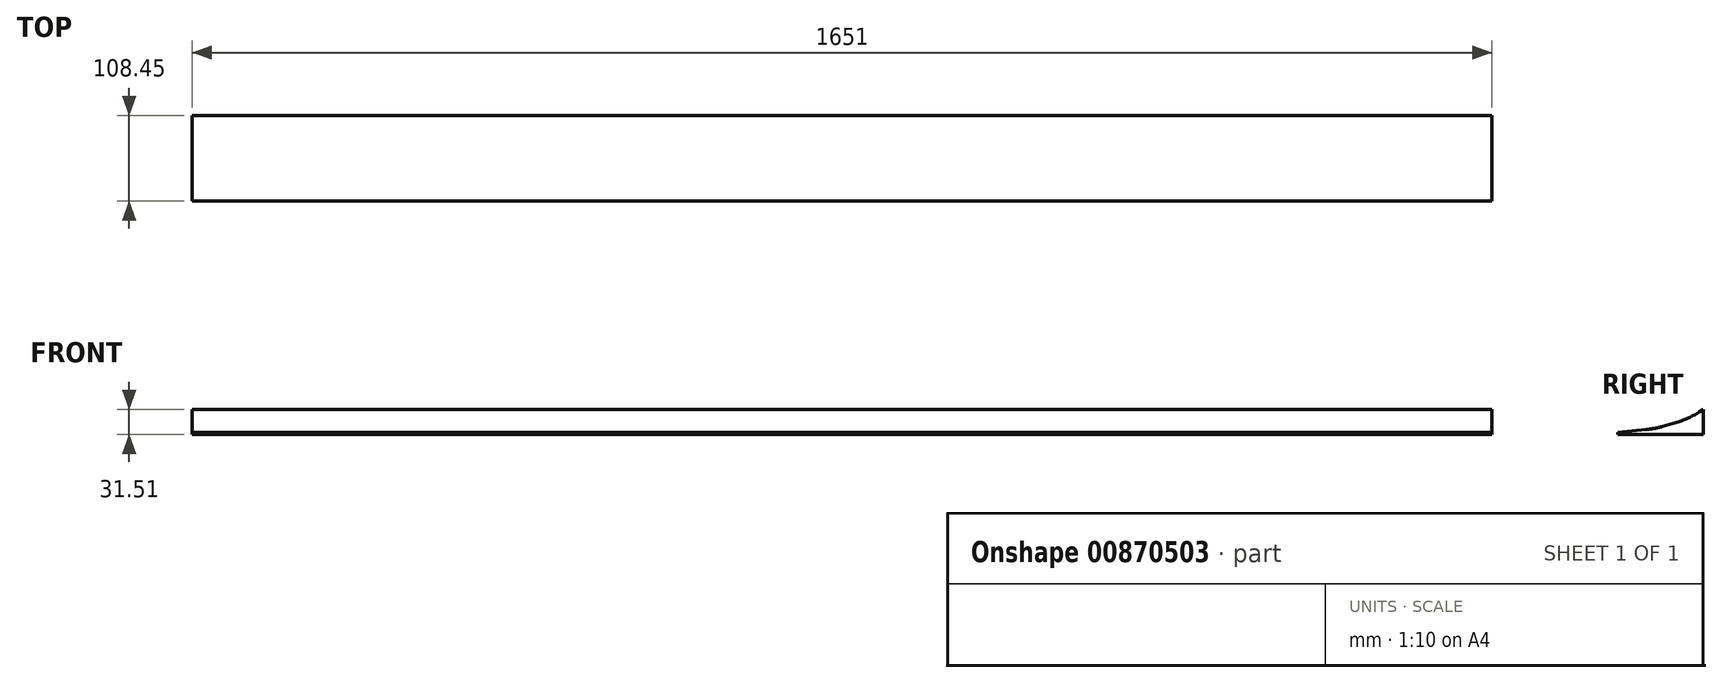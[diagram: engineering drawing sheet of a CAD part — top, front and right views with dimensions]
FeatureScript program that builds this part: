
annotation { "Feature Type Name" : "Feature", "Feature Type Description" : "" }
export const myFeature = defineFeature(function(context is Context, id is Id, definition is map)
    precondition{}
    {
        {
            var Q0;
            Q0=qCreatedBy(makeId("Right.planeOp"),FACE);
            var sketch = newSketch(context, id + "F0", { "sketchPlane" : qUnion([Q0])});
            skLineSegment(sketch, "E0", {"start": v(-52.82, 2.3) * mm, "end": v(-17.4, 5.94) * mm});
            skLineSegment(sketch, "E1", {"start": v(3.6, 9.9) * mm, "end": v(17.23, 13.68) * mm});
            skLineSegment(sketch, "E2", {"start": v(50.59, 28.36) * mm, "end": v(55.63, 31.51) * mm});
            skLineSegment(sketch, "E3", {"start": v(55.63, 31.51) * mm, "end": v(55.63, 0) * mm});
            skLineSegment(sketch, "E4", {"start": v(55.63, 0) * mm, "end": v(-52.82, 0) * mm});
            skLineSegment(sketch, "E5", {"start": v(-52.82, 0) * mm, "end": v(-52.82, 2.3) * mm});
            skPoint(sketch, "E6.visualSharp", {"position": v(-6.74, 7.03) * mm});
            skArc(sketch, "E6.filletArc", {"start": v(-17.4, 5.94) * mm, "mid": v(-6.82, 7.47) * mm, "end": v(3.6, 9.9) * mm});
            skPoint(sketch, "E7.visualSharp", {"position": v(34.97, 18.6) * mm});
            skArc(sketch, "E7.filletArc", {"start": v(17.23, 13.68) * mm, "mid": v(34.44, 19.82) * mm, "end": v(50.59, 28.36) * mm});
            skSolve(sketch);
        }
        {
            var Q0;
            Q0 = qSketchRegion(id + "F0", true);
            extrude(context, id + "F1", {"entities" : qUnion([Q0]), "depth" : 1651 * mm, "offsetDistance" : 25.4 * mm, "symmetric" : true});
        }
    });
